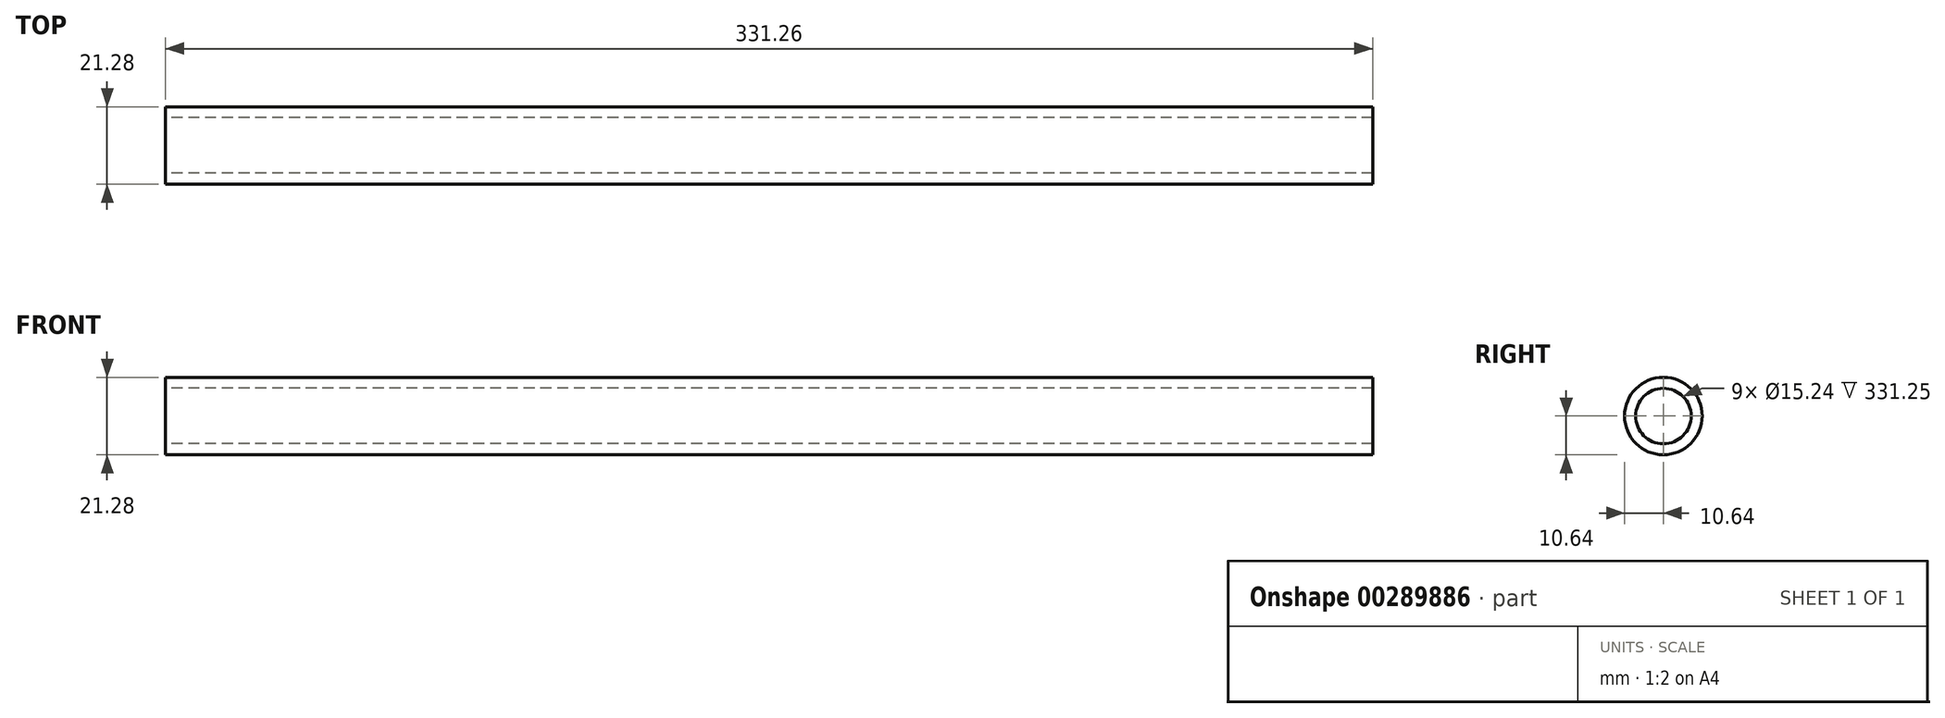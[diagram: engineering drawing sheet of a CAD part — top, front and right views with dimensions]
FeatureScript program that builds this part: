
annotation { "Feature Type Name" : "Feature", "Feature Type Description" : "" }
export const myFeature = defineFeature(function(context is Context, id is Id, definition is map)
    precondition{}
    {
        {
            var Q0;
            Q0=qCreatedBy(makeId("Right.planeOp"),FACE);
            var sketch = newSketch(context, id + "F0", { "sketchPlane" : qUnion([Q0])});
            skCircle(sketch, "E0", {"center": v(0, 0) * mm, "radius": 7.62 * mm});
            skCircle(sketch, "E1", {"center": v(0, 0) * mm, "radius": 10.64 * mm});
            skSolve(sketch);
        }
        {
            var Q0;
            Q0=makeQuery(id+"F0.imprint","IMPRINT",FACE,{"disambiguationData":[TD([[makeQuery(id+"F0.imprint","IMPRINT",EDGE,{"derivedFrom":sQuery(id+"F0.wireOp",EDGE,"E0")}),-1.0]])]});
            extrude(context, id + "F1", {"entities" : qUnion([Q0]), "endBound" : BoundingType.SYMMETRIC, "depth" : 279.4 * mm + 7 / 203.2 * mm + 51.82 * mm});
        }
    });
